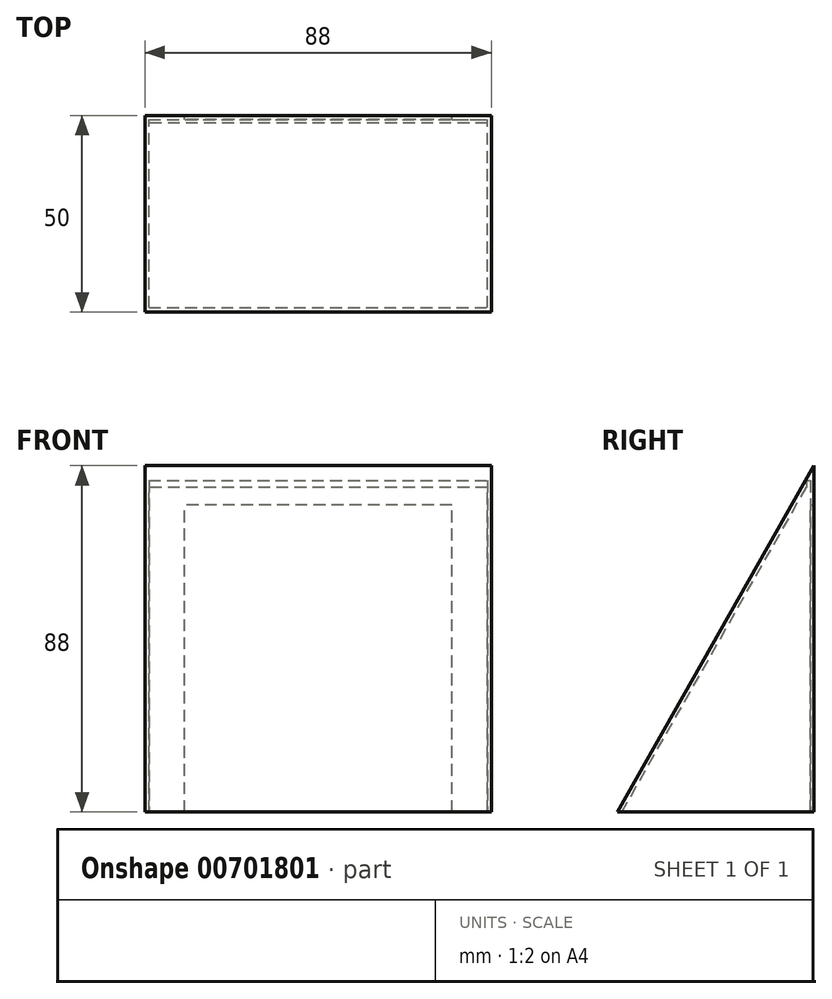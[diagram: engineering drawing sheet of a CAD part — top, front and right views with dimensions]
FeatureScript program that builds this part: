
annotation { "Feature Type Name" : "Feature", "Feature Type Description" : "" }
export const myFeature = defineFeature(function(context is Context, id is Id, definition is map)
    precondition{}
    {
        {
            var Q0;
            Q0=qCreatedBy(makeId("Front.planeOp"),FACE);
            var sketch = newSketch(context, id + "F0", { "sketchPlane" : qUnion([Q0])});
            skLineSegment(sketch, "E0.bottom", {"start": v(-44, 44) * mm, "end": v(44, 44) * mm});
            skLineSegment(sketch, "E0.top", {"start": v(-44, -44) * mm, "end": v(44, -44) * mm});
            skLineSegment(sketch, "E0.left", {"start": v(-44, 44) * mm, "end": v(-44, -44) * mm});
            skLineSegment(sketch, "E0.right", {"start": v(44, 44) * mm, "end": v(44, -44) * mm});
            skPoint(sketch, "E0.middle", {"position": v(0, 0) * mm});
            skSolve(sketch);
        }
        {
            var Q0;
            Q0 = qSketchRegion(id + "F0", true);
            extrude(context, id + "F1", {"entities" : qUnion([Q0]), "endBound" : BoundingType.SYMMETRIC, "depth" : 50 * mm, "offsetDistance" : 25 * mm});
        }
        {
            var Q0;
            Q0=qCreatedBy(makeId("Right.planeOp"),FACE);
            var sketch = newSketch(context, id + "F2", { "sketchPlane" : qUnion([Q0])});
            skLineSegment(sketch, "E1", {"start": v(25, 44) * mm, "end": v(-25, 44) * mm});
            skLineSegment(sketch, "E2", {"start": v(-25, 44) * mm, "end": v(-25, -44) * mm});
            skLineSegment(sketch, "E3", {"start": v(-25, -44) * mm, "end": v(25, 44) * mm});
            skSolve(sketch);
        }
        {
            var Q0;
            Q0 = qSketchRegion(id + "F2", true);
            extrude(context, id + "F3", {"entities" : qUnion([Q0]), "operationType" : NewBodyOperationType.REMOVE, "endBound" : BoundingType.SYMMETRIC, "oppositeDirection" : true, "depth" : 100 * mm, "offsetDistance" : 25 * mm});
        }
        {
            var Q0;
            Q0=makeQuery(id+"F1.opExtrude","SWEPT_FACE",FACE,{"disambiguationData":[OSD([sQuery(id+"F0.wireOp",EDGE,"E0.top")])]});
            shell(context, id + "F4", {"entities" : qUnion([Q0]), "thickness" : 1 * mm});
        }
        {
            var Q0;
            Q0=makeQuery(id+"F1.opExtrude","CAP_FACE",FACE,{"disambiguationData":[OSD([sQuery(id+"F0.wireOp",EDGE,"E0.bottom"),sQuery(id+"F0.wireOp",EDGE,"E0.top"),sQuery(id+"F0.wireOp",EDGE,"E0.left"),sQuery(id+"F0.wireOp",EDGE,"E0.right")])],"isStart":true});
            var sketch = newSketch(context, id + "F5", { "sketchPlane" : qUnion([Q0])});
            skLineSegment(sketch, "E4.bottom", {"start": v(-34, -44) * mm, "end": v(34, -44) * mm});
            skLineSegment(sketch, "E4.top", {"start": v(-34, 34) * mm, "end": v(34, 34) * mm});
            skLineSegment(sketch, "E4.left", {"start": v(-34, -44) * mm, "end": v(-34, 34) * mm});
            skLineSegment(sketch, "E4.right", {"start": v(34, -44) * mm, "end": v(34, 34) * mm});
            skSolve(sketch);
        }
        {
            var Q0;
            Q0 = qSketchRegion(id + "F5", true);
            var Q1;
            Q1=makeQuery(id+"F4.opShell","OFFSET_FACE",FACE,{"disambiguationData":[OSD([sQuery(id+"F0.wireOp",EDGE,"E0.bottom"),sQuery(id+"F0.wireOp",EDGE,"E0.top"),sQuery(id+"F0.wireOp",EDGE,"E0.left"),sQuery(id+"F0.wireOp",EDGE,"E0.right")])]});
            extrude(context, id + "F6", {"entities" : qUnion([Q0, Q1]), "operationType" : NewBodyOperationType.REMOVE, "oppositeDirection" : true, "depth" : 1 * mm, "offsetDistance" : 25 * mm});
        }
    });
